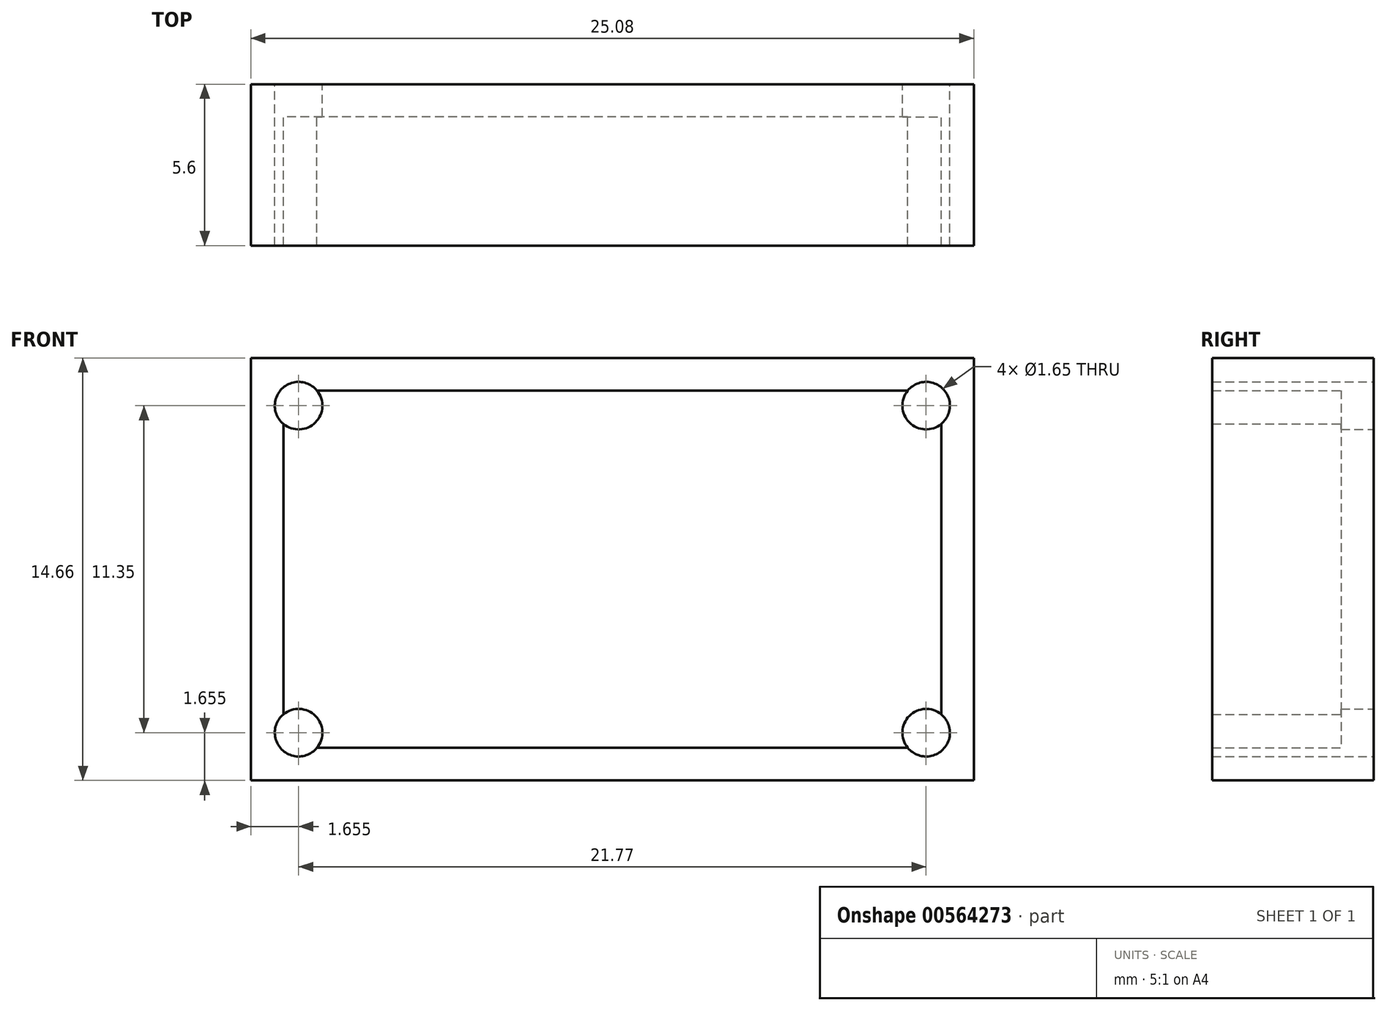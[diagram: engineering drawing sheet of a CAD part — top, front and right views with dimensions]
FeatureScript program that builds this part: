
annotation { "Feature Type Name" : "Feature", "Feature Type Description" : "" }
export const myFeature = defineFeature(function(context is Context, id is Id, definition is map)
    precondition{}
    {
        {
            var Q0;
            Q0=qCreatedBy(makeId("Front.planeOp"),FACE);
            var sketch = newSketch(context, id + "F0", { "sketchPlane" : qUnion([Q0])});
            skLineSegment(sketch, "E0.bottom", {"start": v(11.4, 6.2) * mm, "end": v(-11.4, 6.2) * mm});
            skLineSegment(sketch, "E0.top", {"start": v(11.4, -6.2) * mm, "end": v(-11.4, -6.2) * mm});
            skLineSegment(sketch, "E0.left", {"start": v(11.4, 6.2) * mm, "end": v(11.41, -6.2) * mm});
            skLineSegment(sketch, "E0.right", {"start": v(-11.41, 6.2) * mm, "end": v(-11.4, -6.2) * mm});
            skPoint(sketch, "E0.middle", {"position": v(0, 0) * mm});
            skLineSegment(sketch, "E1.0", {"start": v(12.54, 7.33) * mm, "end": v(-12.54, 7.33) * mm});
            skLineSegment(sketch, "E1.1", {"start": v(12.54, 7.33) * mm, "end": v(12.54, -7.33) * mm});
            skLineSegment(sketch, "E1.2", {"start": v(12.54, -7.33) * mm, "end": v(-12.54, -7.33) * mm});
            skLineSegment(sketch, "E1.3", {"start": v(-12.54, 7.33) * mm, "end": v(-12.54, -7.33) * mm});
            skCircle(sketch, "E2", {"center": v(-10.89, 5.68) * mm, "radius": 0.53 * mm});
            skCircle(sketch, "E3.0", {"center": v(-10.89, 5.68) * mm, "radius": 0.82 * mm});
            skPoint(sketch, "E4", {"position": v(-10.89, 5.15) * mm});
            skPoint(sketch, "E5", {"position": v(-10.36, 5.68) * mm});
            skPoint(sketch, "E6", {"position": v(-11.41, 5.68) * mm});
            skPoint(sketch, "E7", {"position": v(-10.89, 6.2) * mm});
            skCircle(sketch, "E8.MirrorC", {"center": v(10.89, 5.68) * mm, "radius": 0.82 * mm});
            skCircle(sketch, "E9.MirrorC", {"center": v(10.89, 5.68) * mm, "radius": 0.53 * mm});
            skPoint(sketch, "E10.MirrorP", {"position": v(10.89, 5.15) * mm});
            skPoint(sketch, "E11.MirrorP", {"position": v(10.36, 5.68) * mm});
            skPoint(sketch, "E12.MirrorP", {"position": v(10.89, 6.2) * mm});
            skPoint(sketch, "E13.MirrorP", {"position": v(11.41, 5.68) * mm});
            skCircle(sketch, "E14.MirrorC", {"center": v(10.89, -5.68) * mm, "radius": 0.82 * mm});
            skPoint(sketch, "E15.MirrorP", {"position": v(10.89, -5.15) * mm});
            skPoint(sketch, "E16.MirrorP", {"position": v(10.36, -5.68) * mm});
            skPoint(sketch, "E17.MirrorP", {"position": v(10.89, -6.2) * mm});
            skPoint(sketch, "E18.MirrorP", {"position": v(11.41, -5.68) * mm});
            skLineSegment(sketch, "E19.MirrorCS", {"start": v(11.4, -6.2) * mm, "end": v(11.41, 6.2) * mm});
            skCircle(sketch, "E20.MirrorC", {"center": v(10.89, -5.68) * mm, "radius": 0.53 * mm});
            skPoint(sketch, "E21.MirrorP", {"position": v(-10.89, -5.15) * mm});
            skCircle(sketch, "E22.MirrorC", {"center": v(-10.89, -5.68) * mm, "radius": 0.82 * mm});
            skCircle(sketch, "E23.MirrorC", {"center": v(-10.89, -5.68) * mm, "radius": 0.53 * mm});
            skPoint(sketch, "E24.MirrorP", {"position": v(-10.36, -5.68) * mm});
            skPoint(sketch, "E25.MirrorP", {"position": v(-10.89, -6.2) * mm});
            skPoint(sketch, "E26.MirrorP", {"position": v(-11.41, -5.68) * mm});
            skSolve(sketch);
        }
        {
            var Q0;
            Q0 = qSketchRegion(id + "F0", true);
            extrude(context, id + "F1", {"entities" : qUnion([Q0]), "depth" : 5.6 * mm, "offsetDistance" : 25 * mm});
        }
        {
            var Q0;
            Q0 = qSketchRegion(id + "F0", true);
            var Q1;
            {var subQ1=sQuery(id+"F0.wireOp",EDGE,"E0.bottom");var subQ13=sQuery(id+"F0.wireOp",EDGE,"E8.MirrorC");var subQ15=makeQuery(id+"F0.imprint","INTERSECT",VERTEX,{"derivedFrom":[subQ1,subQ13]});Q1=makeQuery(id+"F0.imprint","IMPRINT",FACE,{"disambiguationData":[TD([[makeQuery(id+"F0.imprint","IMPRINT",EDGE,{"disambiguationData":[TD([[subQ15,-1.0]])],"derivedFrom":subQ1}),1.0]])]});}
            extrude(context, id + "F2", {"entities" : qUnion([Q0, Q1]), "operationType" : NewBodyOperationType.ADD, "depth" : 1.13 * mm, "offsetDistance" : 25 * mm});
        }
    });
